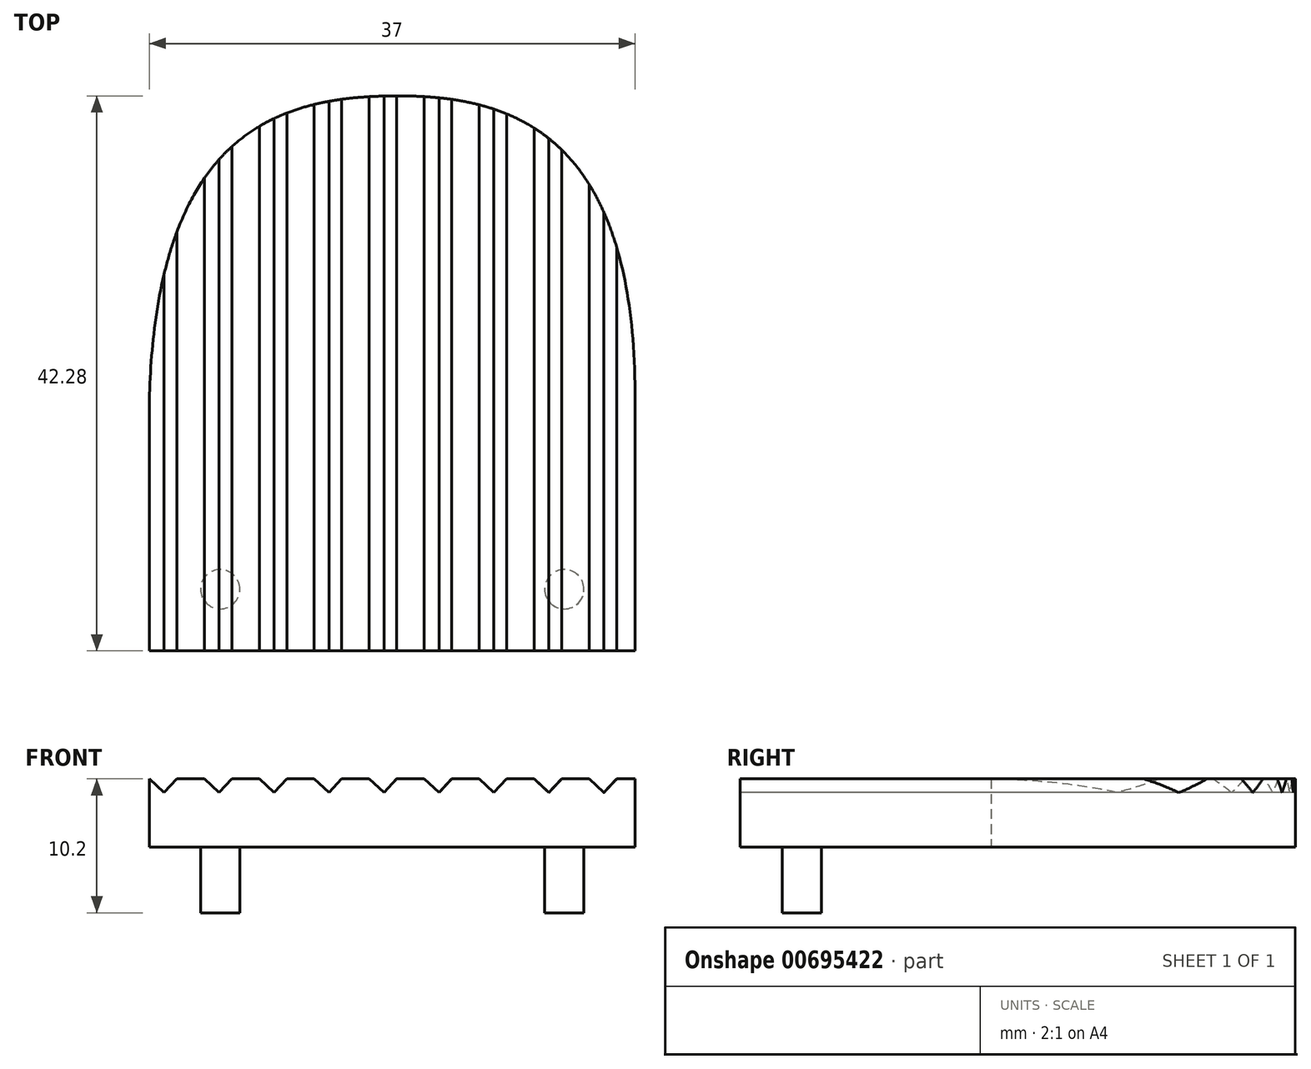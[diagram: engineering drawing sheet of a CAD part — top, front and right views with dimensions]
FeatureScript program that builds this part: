
annotation { "Feature Type Name" : "Feature", "Feature Type Description" : "" }
export const myFeature = defineFeature(function(context is Context, id is Id, definition is map)
    precondition{}
    {
        {
            var Q0;
            Q0=qCreatedBy(makeId("Top.planeOp"),FACE);
            var sketch = newSketch(context, id + "F0", { "sketchPlane" : qUnion([Q0])});
            skLineSegment(sketch, "E0", {"start": v(-17.92, -45.08) * mm, "end": v(19.08, -45.08) * mm});
            skLineSegment(sketch, "E1", {"start": v(0.58, -45.08) * mm, "end": v(0.58, -2.8) * mm});
            skLineSegment(sketch, "E2", {"start": v(19.08, -45.08) * mm, "end": v(19.08, -25.98) * mm});
            skLineSegment(sketch, "E3", {"start": v(-17.92, -45.08) * mm, "end": v(-17.92, -25.98) * mm});
            skFitSpline(sketch, "E4", {"points": [v(-17.92, -25.98) * mm, v(0.58, -2.8) * mm, v(19.08, -25.98) * mm], "startDerivative": vector(3.13, 120.27) * mm, "endDerivative": vector(-0.15, -122.53) * mm});
            skSolve(sketch);
        }
        {
            var Q0;
            {var subQ2=sQuery(id+"F0.wireOp",EDGE,"E1");Q0=makeQuery(id+"F0.imprint","IMPRINT",FACE,{"disambiguationData":[TD([[makeQuery(id+"F0.imprint","IMPRINT",EDGE,{"derivedFrom":subQ2}),-1.0]])]});}
            var Q1;
            {var subQ2=sQuery(id+"F0.wireOp",EDGE,"E1");Q1=makeQuery(id+"F0.imprint","IMPRINT",FACE,{"disambiguationData":[TD([[makeQuery(id+"F0.imprint","IMPRINT",EDGE,{"derivedFrom":subQ2}),1.0]])]});}
            extrude(context, id + "F1", {"entities" : qUnion([Q0, Q1]), "depth" : 5.2 * mm, "offsetDistance" : 25 * mm});
        }
        {
            var Q0;
            Q0=makeQuery(id+"F1.opExtrude","CAP_FACE",FACE,{"disambiguationData":[OSD([sQuery(id+"F0.wireOp",EDGE,"E0"),sQuery(id+"F0.wireOp",EDGE,"E2"),sQuery(id+"F0.wireOp",EDGE,"E3"),sQuery(id+"F0.wireOp",EDGE,"E4")])],"isStart":true});
            var sketch = newSketch(context, id + "F2", { "sketchPlane" : qUnion([Q0])});
            skLineSegment(sketch, "E5", {"start": v(-17.92, 41.88) * mm, "end": v(-14.02, 41.88) * mm});
            skLineSegment(sketch, "E6", {"start": v(-14.02, 41.88) * mm, "end": v(-14.02, 45.08) * mm});
            skCircle(sketch, "E7", {"center": v(-12.52, 40.38) * mm, "radius": 1.5 * mm});
            skLineSegment(sketch, "E8", {"start": v(19.08, 45.08) * mm, "end": v(15.18, 45.08) * mm});
            skLineSegment(sketch, "E9", {"start": v(15.18, 45.08) * mm, "end": v(15.18, 41.88) * mm});
            skCircle(sketch, "E10", {"center": v(13.68, 40.38) * mm, "radius": 1.5 * mm});
            skSolve(sketch);
        }
        {
            var Q0;
            Q0 = qSketchRegion(id + "F2", true);
            extrude(context, id + "F3", {"entities" : qUnion([Q0]), "operationType" : NewBodyOperationType.ADD, "depth" : 5 * mm, "offsetDistance" : 25 * mm});
        }
        {
            var Q0;
            Q0=makeQuery(id+"F1.opExtrude","SWEPT_FACE",FACE,{"disambiguationData":[OSD([sQuery(id+"F0.wireOp",EDGE,"E0")])]});
            var sketch = newSketch(context, id + "F4", { "sketchPlane" : qUnion([Q0])});
            skLineSegment(sketch, "E11", {"start": v(-17.92, 5.2) * mm, "end": v(-16.8, 4.16) * mm});
            skLineSegment(sketch, "E12", {"start": v(-16.8, 4.16) * mm, "end": v(-15.82, 5.2) * mm});
            skLineSegment(sketch, "E13", {"start": v(-15.82, 5.2) * mm, "end": v(-14.7, 4.16) * mm});
            skLineSegment(sketch, "E14", {"start": v(-14.7, 4.16) * mm, "end": v(-13.73, 5.2) * mm});
            skLineSegment(sketch, "E15", {"start": v(-13.73, 5.2) * mm, "end": v(-12.6, 4.16) * mm});
            skLineSegment(sketch, "E16", {"start": v(-12.6, 4.16) * mm, "end": v(-11.64, 5.2) * mm});
            skLineSegment(sketch, "E17", {"start": v(-11.64, 5.2) * mm, "end": v(-10.51, 4.16) * mm});
            skLineSegment(sketch, "E18", {"start": v(-10.51, 4.16) * mm, "end": v(-9.54, 5.2) * mm});
            skLineSegment(sketch, "E19", {"start": v(-9.54, 5.2) * mm, "end": v(-8.42, 4.16) * mm});
            skLineSegment(sketch, "E20", {"start": v(-8.42, 4.16) * mm, "end": v(-7.45, 5.2) * mm});
            skLineSegment(sketch, "E21", {"start": v(-7.45, 5.2) * mm, "end": v(-6.33, 4.16) * mm});
            skLineSegment(sketch, "E22", {"start": v(-6.33, 4.16) * mm, "end": v(-5.36, 5.2) * mm});
            skLineSegment(sketch, "E23", {"start": v(-5.36, 5.2) * mm, "end": v(-4.23, 4.16) * mm});
            skLineSegment(sketch, "E24", {"start": v(-4.23, 4.16) * mm, "end": v(-3.26, 5.2) * mm});
            skLineSegment(sketch, "E25", {"start": v(-3.26, 5.2) * mm, "end": v(-2.14, 4.16) * mm});
            skLineSegment(sketch, "E26", {"start": v(-2.14, 4.16) * mm, "end": v(-1.17, 5.2) * mm});
            skLineSegment(sketch, "E27", {"start": v(-1.17, 5.2) * mm, "end": v(-0.05, 4.16) * mm});
            skLineSegment(sketch, "E28", {"start": v(-0.05, 4.16) * mm, "end": v(0.93, 5.2) * mm});
            skLineSegment(sketch, "E29", {"start": v(0.93, 5.2) * mm, "end": v(2.05, 4.16) * mm});
            skLineSegment(sketch, "E30", {"start": v(2.05, 4.16) * mm, "end": v(3.02, 5.2) * mm});
            skLineSegment(sketch, "E31", {"start": v(3.02, 5.2) * mm, "end": v(4.14, 4.16) * mm});
            skLineSegment(sketch, "E32", {"start": v(4.14, 4.16) * mm, "end": v(5.11, 5.2) * mm});
            skLineSegment(sketch, "E33", {"start": v(5.11, 5.2) * mm, "end": v(6.23, 4.16) * mm});
            skLineSegment(sketch, "E34", {"start": v(6.23, 4.16) * mm, "end": v(7.2, 5.2) * mm});
            skLineSegment(sketch, "E35", {"start": v(7.2, 5.2) * mm, "end": v(8.33, 4.16) * mm});
            skLineSegment(sketch, "E36", {"start": v(8.33, 4.16) * mm, "end": v(9.3, 5.2) * mm});
            skLineSegment(sketch, "E37", {"start": v(9.3, 5.2) * mm, "end": v(10.42, 4.16) * mm});
            skLineSegment(sketch, "E38", {"start": v(10.42, 4.16) * mm, "end": v(11.4, 5.2) * mm});
            skLineSegment(sketch, "E39", {"start": v(11.4, 5.2) * mm, "end": v(12.51, 4.16) * mm});
            skLineSegment(sketch, "E40", {"start": v(12.51, 4.16) * mm, "end": v(13.49, 5.2) * mm});
            skLineSegment(sketch, "E41", {"start": v(13.49, 5.2) * mm, "end": v(14.6, 4.16) * mm});
            skLineSegment(sketch, "E42", {"start": v(14.6, 4.16) * mm, "end": v(15.58, 5.2) * mm});
            skLineSegment(sketch, "E43", {"start": v(15.58, 5.2) * mm, "end": v(16.7, 4.16) * mm});
            skLineSegment(sketch, "E44", {"start": v(16.7, 4.16) * mm, "end": v(17.67, 5.2) * mm});
            skLineSegment(sketch, "E45", {"start": v(17.67, 5.2) * mm, "end": v(19.46, 3.54) * mm});
            skLineSegment(sketch, "E46", {"start": v(19.46, 3.54) * mm, "end": v(19.46, 5.2) * mm});
            skLineSegment(sketch, "E47", {"start": v(19.46, 5.2) * mm, "end": v(-17.92, 5.2) * mm});
            skSolve(sketch);
        }
        {
            var Q0;
            {var subQ0=sQuery(id+"F4.wireOp",EDGE,"E11");Q0=makeQuery(id+"F4.imprint","IMPRINT",FACE,{"disambiguationData":[TD([[makeQuery(id+"F4.imprint","IMPRINT",EDGE,{"derivedFrom":subQ0}),1.0]])]});}
            var Q1;
            {var subQ0=sQuery(id+"F4.wireOp",EDGE,"E15");Q1=makeQuery(id+"F4.imprint","IMPRINT",FACE,{"disambiguationData":[TD([[makeQuery(id+"F4.imprint","IMPRINT",EDGE,{"derivedFrom":subQ0}),1.0]])]});}
            var Q2;
            {var subQ0=sQuery(id+"F4.wireOp",EDGE,"E19");Q2=makeQuery(id+"F4.imprint","IMPRINT",FACE,{"disambiguationData":[TD([[makeQuery(id+"F4.imprint","IMPRINT",EDGE,{"derivedFrom":subQ0}),1.0]])]});}
            var Q3;
            {var subQ0=sQuery(id+"F4.wireOp",EDGE,"E23");Q3=makeQuery(id+"F4.imprint","IMPRINT",FACE,{"disambiguationData":[TD([[makeQuery(id+"F4.imprint","IMPRINT",EDGE,{"derivedFrom":subQ0}),1.0]])]});}
            var Q4;
            {var subQ0=sQuery(id+"F4.wireOp",EDGE,"E27");Q4=makeQuery(id+"F4.imprint","IMPRINT",FACE,{"disambiguationData":[TD([[makeQuery(id+"F4.imprint","IMPRINT",EDGE,{"derivedFrom":subQ0}),1.0]])]});}
            var Q5;
            {var subQ0=sQuery(id+"F4.wireOp",EDGE,"E31");Q5=makeQuery(id+"F4.imprint","IMPRINT",FACE,{"disambiguationData":[TD([[makeQuery(id+"F4.imprint","IMPRINT",EDGE,{"derivedFrom":subQ0}),1.0]])]});}
            var Q6;
            {var subQ0=sQuery(id+"F4.wireOp",EDGE,"E35");Q6=makeQuery(id+"F4.imprint","IMPRINT",FACE,{"disambiguationData":[TD([[makeQuery(id+"F4.imprint","IMPRINT",EDGE,{"derivedFrom":subQ0}),1.0]])]});}
            var Q7;
            {var subQ0=sQuery(id+"F4.wireOp",EDGE,"E39");Q7=makeQuery(id+"F4.imprint","IMPRINT",FACE,{"disambiguationData":[TD([[makeQuery(id+"F4.imprint","IMPRINT",EDGE,{"derivedFrom":subQ0}),1.0]])]});}
            var Q8;
            {var subQ0=sQuery(id+"F4.wireOp",EDGE,"E43");Q8=makeQuery(id+"F4.imprint","IMPRINT",FACE,{"disambiguationData":[TD([[makeQuery(id+"F4.imprint","IMPRINT",EDGE,{"derivedFrom":subQ0}),1.0]])]});}
            extrude(context, id + "F5", {"entities" : qUnion([Q0, Q1, Q2, Q3, Q4, Q5, Q6, Q7, Q8]), "operationType" : NewBodyOperationType.REMOVE, "oppositeDirection" : true, "depth" : 47.5 * mm, "offsetDistance" : 25 * mm});
        }
    });
